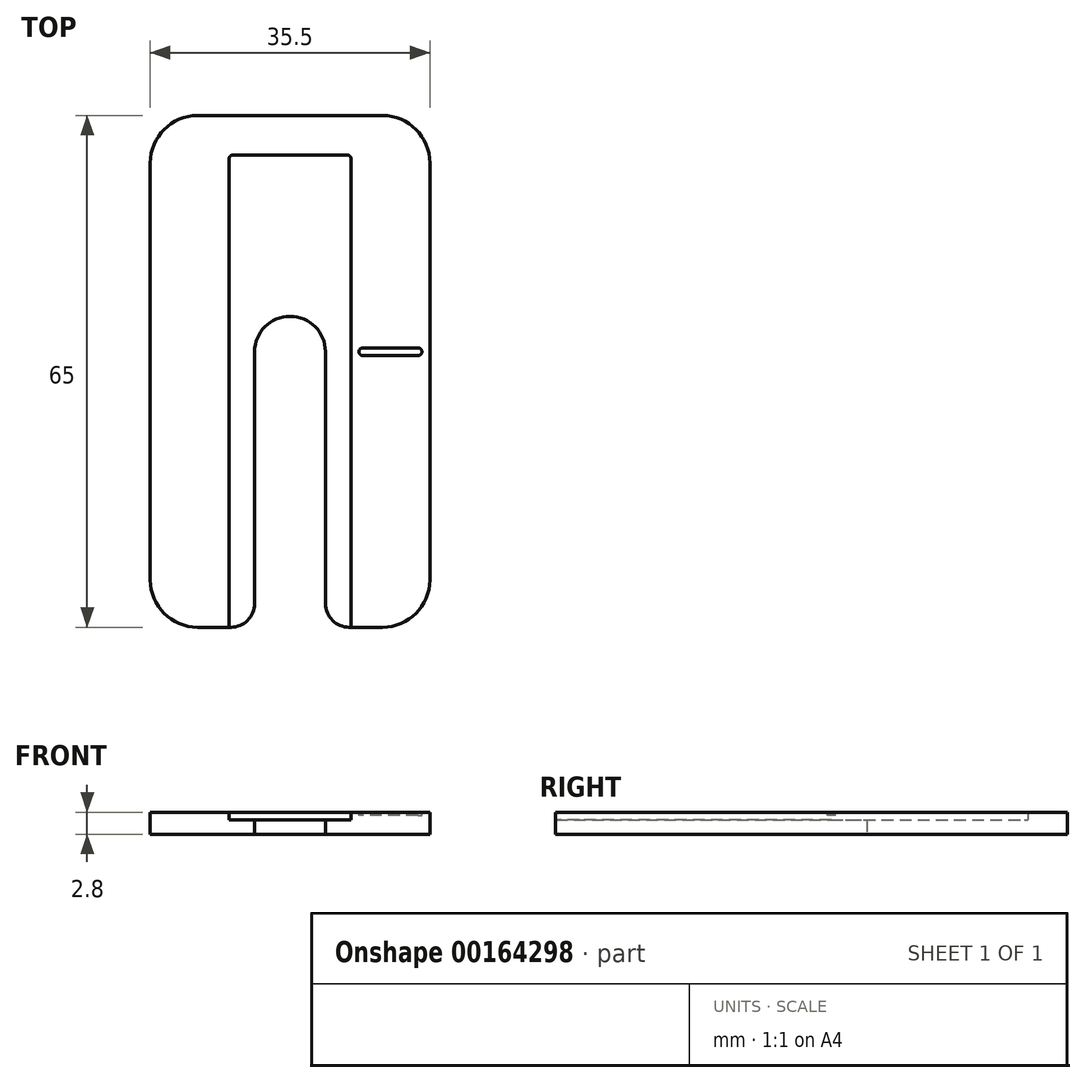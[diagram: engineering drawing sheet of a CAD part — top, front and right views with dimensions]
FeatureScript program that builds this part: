
annotation { "Feature Type Name" : "Feature", "Feature Type Description" : "" }
export const myFeature = defineFeature(function(context is Context, id is Id, definition is map)
    precondition{}
    {
        {
            assignVariable(context, id + "F0", {"name" : "Height", "anyValue" : 1.8});
        }
        {
            var Q0;
            Q0=qCreatedBy(makeId("Top.planeOp"),FACE);
            cPlane(context, id + "F1", {"entities" : qUnion([Q0]), "cplaneType" : CPlaneType.OFFSET, "offset" : (getVariable(context, 'Height')) * mm, "width" : 150 * mm, "height" : 150 * mm});
        }
        {
            var Q0;
            Q0=qCreatedBy(makeId("Top.planeOp"),FACE);
            var sketch = newSketch(context, id + "F2", { "sketchPlane" : qUnion([Q0])});
            skLineSegment(sketch, "E0.bottom", {"start": v(17.75, -32.5) * mm, "end": v(4.5, -32.5) * mm});
            skLineSegment(sketch, "E0.top", {"start": v(17.75, 32.5) * mm, "end": v(-17.75, 32.5) * mm});
            skLineSegment(sketch, "E0.left", {"start": v(17.75, -32.5) * mm, "end": v(17.75, 32.5) * mm});
            skLineSegment(sketch, "E0.right", {"start": v(-17.75, -32.5) * mm, "end": v(-17.75, 32.5) * mm});
            skPoint(sketch, "E0.middle", {"position": v(0, 0) * mm});
            skArc(sketch, "E1", {"start": v(4.5, 2.5) * mm, "mid": v(0, 7) * mm, "end": v(-4.5, 2.5) * mm});
            skLineSegment(sketch, "E2", {"start": v(-4.5, 2.5) * mm, "end": v(-4.5, -32.5) * mm});
            skLineSegment(sketch, "E3", {"start": v(4.5, 2.5) * mm, "end": v(4.5, -32.5) * mm});
            skLineSegment(sketch, "E4.trimOffspring", {"start": v(-4.5, -32.5) * mm, "end": v(-17.75, -32.5) * mm});
            skSolve(sketch);
        }
        {
            var Q0;
            Q0 = qSketchRegion(id + "F2", true);
            extrude(context, id + "F3", {"entities" : qUnion([Q0]), "depth" : (getVariable(context, 'Height') + 1) * mm});
        }
        {
            var Q0;
            Q0=qCreatedBy(id+"F1.planeOp",FACE);
            var sketch = newSketch(context, id + "F4", { "sketchPlane" : qUnion([Q0])});
            skLineSegment(sketch, "E5.bottom", {"start": v(7.75, -32.5) * mm, "end": v(-7.75, -32.5) * mm});
            skLineSegment(sketch, "E5.top", {"start": v(7.75, 27.5) * mm, "end": v(-7.75, 27.5) * mm});
            skLineSegment(sketch, "E5.left", {"start": v(7.75, -32.5) * mm, "end": v(7.75, 27.5) * mm});
            skLineSegment(sketch, "E5.right", {"start": v(-7.75, -32.5) * mm, "end": v(-7.75, 27.5) * mm});
            skPoint(sketch, "E5.middle", {"position": v(0, -2.5) * mm});
            skSolve(sketch);
        }
        {
            var Q0;
            Q0 = qSketchRegion(id + "F4", true);
            extrude(context, id + "F5", {"entities" : qUnion([Q0]), "operationType" : NewBodyOperationType.REMOVE, "depth" : 25 * mm});
        }
        {
            var Q0;
            Q0=makeQuery(id+"F3.opExtrude","CAP_FACE",FACE,{"disambiguationData":[OSD([sQuery(id+"F2.wireOp",EDGE,"E0.bottom"),sQuery(id+"F2.wireOp",EDGE,"E0.top"),sQuery(id+"F2.wireOp",EDGE,"E0.left"),sQuery(id+"F2.wireOp",EDGE,"E0.right"),sQuery(id+"F2.wireOp",EDGE,"E1"),sQuery(id+"F2.wireOp",EDGE,"E2"),sQuery(id+"F2.wireOp",EDGE,"E3"),sQuery(id+"F2.wireOp",EDGE,"E4.trimOffspring")])],"isStart":false});
            var sketch = newSketch(context, id + "F6", { "sketchPlane" : qUnion([Q0])});
            skLineSegment(sketch, "E6", {"start": v(0, 2.5) * mm, "end": v(7.75, 2.5) * mm, "construction": true});
            skLineSegment(sketch, "E7", {"start": v(7.75, 2.5) * mm, "end": v(17.75, 2.5) * mm, "construction": true});
            skLineSegment(sketch, "E8.bottom", {"start": v(16.25, 2) * mm, "end": v(9.25, 2) * mm});
            skLineSegment(sketch, "E8.top", {"start": v(16.25, 3) * mm, "end": v(9.25, 3) * mm});
            skLineSegment(sketch, "E8.left", {"start": v(16.25, 2) * mm, "end": v(16.25, 3) * mm, "construction": true});
            skLineSegment(sketch, "E8.right", {"start": v(9.25, 2) * mm, "end": v(9.25, 3) * mm, "construction": true});
            skPoint(sketch, "E8.middle", {"position": v(12.75, 2.5) * mm});
            skArc(sketch, "E9", {"start": v(9.25, 3) * mm, "mid": v(8.75, 2.5) * mm, "end": v(9.25, 2) * mm});
            skArc(sketch, "E10", {"start": v(16.25, 2) * mm, "mid": v(16.75, 2.5) * mm, "end": v(16.25, 3) * mm});
            skSolve(sketch);
        }
        {
            var Q0;
            Q0 = qSketchRegion(id + "F6", true);
            extrude(context, id + "F7", {"entities" : qUnion([Q0]), "operationType" : NewBodyOperationType.REMOVE, "oppositeDirection" : true, "depth" : 0.4 * mm});
        }
        {
            var Q0;
            Q0=makeQuery(id+"F3.opExtrude","SWEPT_EDGE",EDGE,{"disambiguationData":[OSD([sQuery(id+"F2.wireOp",EDGE,"E0.right"),sQuery(id+"F2.wireOp",EDGE,"E4.trimOffspring")])]});
            var Q1;
            Q1=makeQuery(id+"F3.opExtrude","SWEPT_EDGE",EDGE,{"disambiguationData":[OSD([sQuery(id+"F2.wireOp",EDGE,"E0.bottom"),sQuery(id+"F2.wireOp",EDGE,"E0.left")])]});
            var Q2;
            Q2=makeQuery(id+"F3.opExtrude","SWEPT_EDGE",EDGE,{"disambiguationData":[OSD([sQuery(id+"F2.wireOp",EDGE,"E0.top"),sQuery(id+"F2.wireOp",EDGE,"E0.right")])]});
            var Q3;
            Q3=makeQuery(id+"F3.opExtrude","SWEPT_EDGE",EDGE,{"disambiguationData":[OSD([sQuery(id+"F2.wireOp",EDGE,"E0.top"),sQuery(id+"F2.wireOp",EDGE,"E0.left")])]});
            fillet(context, id + "F8", {"entities" : qUnion([Q0, Q1, Q2, Q3]), "radius" : 6 * mm, "tangentPropagation" : true, "allowEdgeOverflow" : false});
        }
        {
            var Q0;
            Q0=makeQuery(id+"F5.boolean.opBoolean","COPY",EDGE,{"derivedFrom":makeQuery(id+"F5.opExtrude","SWEPT_EDGE",EDGE,{"disambiguationData":[OSD([sQuery(id+"F4.wireOp",EDGE,"E5.top"),sQuery(id+"F4.wireOp",EDGE,"E5.left")])]})});
            var Q1;
            Q1=makeQuery(id+"F5.boolean.opBoolean","COPY",EDGE,{"derivedFrom":makeQuery(id+"F5.opExtrude","SWEPT_EDGE",EDGE,{"disambiguationData":[OSD([sQuery(id+"F4.wireOp",EDGE,"E5.top"),sQuery(id+"F4.wireOp",EDGE,"E5.right")])]})});
            fillet(context, id + "F9", {"entities" : qUnion([Q0, Q1]), "radius" : 0.5 * mm, "tangentPropagation" : true, "allowEdgeOverflow" : false});
        }
        {
            var Q0;
            Q0=makeQuery(id+"F5.boolean.opBoolean","COPY",EDGE,{"derivedFrom":makeQuery(id+"F5.opExtrude","SWEPT_EDGE",EDGE,{"disambiguationData":[OSD([sQuery(id+"F4.wireOp",EDGE,"E5.bottom"),sQuery(id+"F4.wireOp",EDGE,"E5.left")])]})});
            var Q1;
            Q1=makeQuery(id+"F5.boolean.opBoolean","COPY",EDGE,{"derivedFrom":makeQuery(id+"F5.opExtrude","SWEPT_EDGE",EDGE,{"disambiguationData":[OSD([sQuery(id+"F4.wireOp",EDGE,"E5.bottom"),sQuery(id+"F4.wireOp",EDGE,"E5.right")])]})});
            var Q2;
            Q2=makeQuery(id+"F3.opExtrude","SWEPT_EDGE",EDGE,{"disambiguationData":[OSD([sQuery(id+"F2.wireOp",EDGE,"E2"),sQuery(id+"F2.wireOp",EDGE,"E4.trimOffspring")])]});
            var Q3;
            Q3=makeQuery(id+"F3.opExtrude","SWEPT_EDGE",EDGE,{"disambiguationData":[OSD([sQuery(id+"F2.wireOp",EDGE,"E0.bottom"),sQuery(id+"F2.wireOp",EDGE,"E3")])]});
            fillet(context, id + "F10", {"entities" : qUnion([Q0, Q1, Q2, Q3]), "radius" : 3 * mm, "tangentPropagation" : true, "allowEdgeOverflow" : false});
        }
    });
